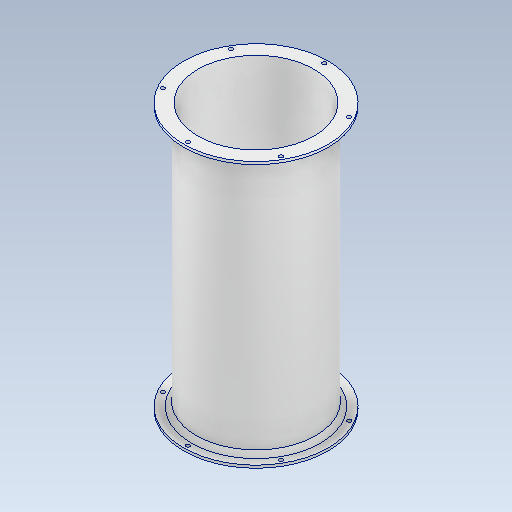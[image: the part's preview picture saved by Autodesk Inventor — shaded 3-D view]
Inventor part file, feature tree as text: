
AUTODESK INVENTOR PART (.ipt)
format: ipt  version: 2021 (Build 250183000, 183)  size: 174,592 bytes
history: native  units: mm
features: revolve x1, hole x1, mirror x1, sketch x1, projected_geometry x1
ambient origin geometry x8: Origin, YZ Plane, XZ Plane, XY Plane, X Axis, Y Axis, Z Axis, Center Point
bodies: Solid1 (feature_tree)
feature tree (5):
  revolve  "Revolution1"  Angle=90.0deg
  hole  "Hole1"  [1 undecoded]
  mirror  "Mirror1"
  sketch  "Sketch2"  dims[d0=300.0mm d3=90.0deg d5=81.5mm d6=2.0mm d7=9.0mm d8=5.0mm d9=45.0deg d10=16.0mm d11=3.0mm d12=3.0mm d13=9.0mm d14=45.0deg d15=5.0mm d16=4.5mm d17=8.0mm d18=60.0mm d20=360.0deg d22=4.5mm d23=10.0mm d24=9.4mm d25=2.0mm d26=90.0deg d27=13.0mm d28=20.594885mm d29=4.5mm]
  projected_geometry  "Projected Loop1"
note: 1 required parameter value undecoded (feature->parameter linkage not recoverable at this tier; creation-order binding heuristic only, values carry confidence <= 0.55)
